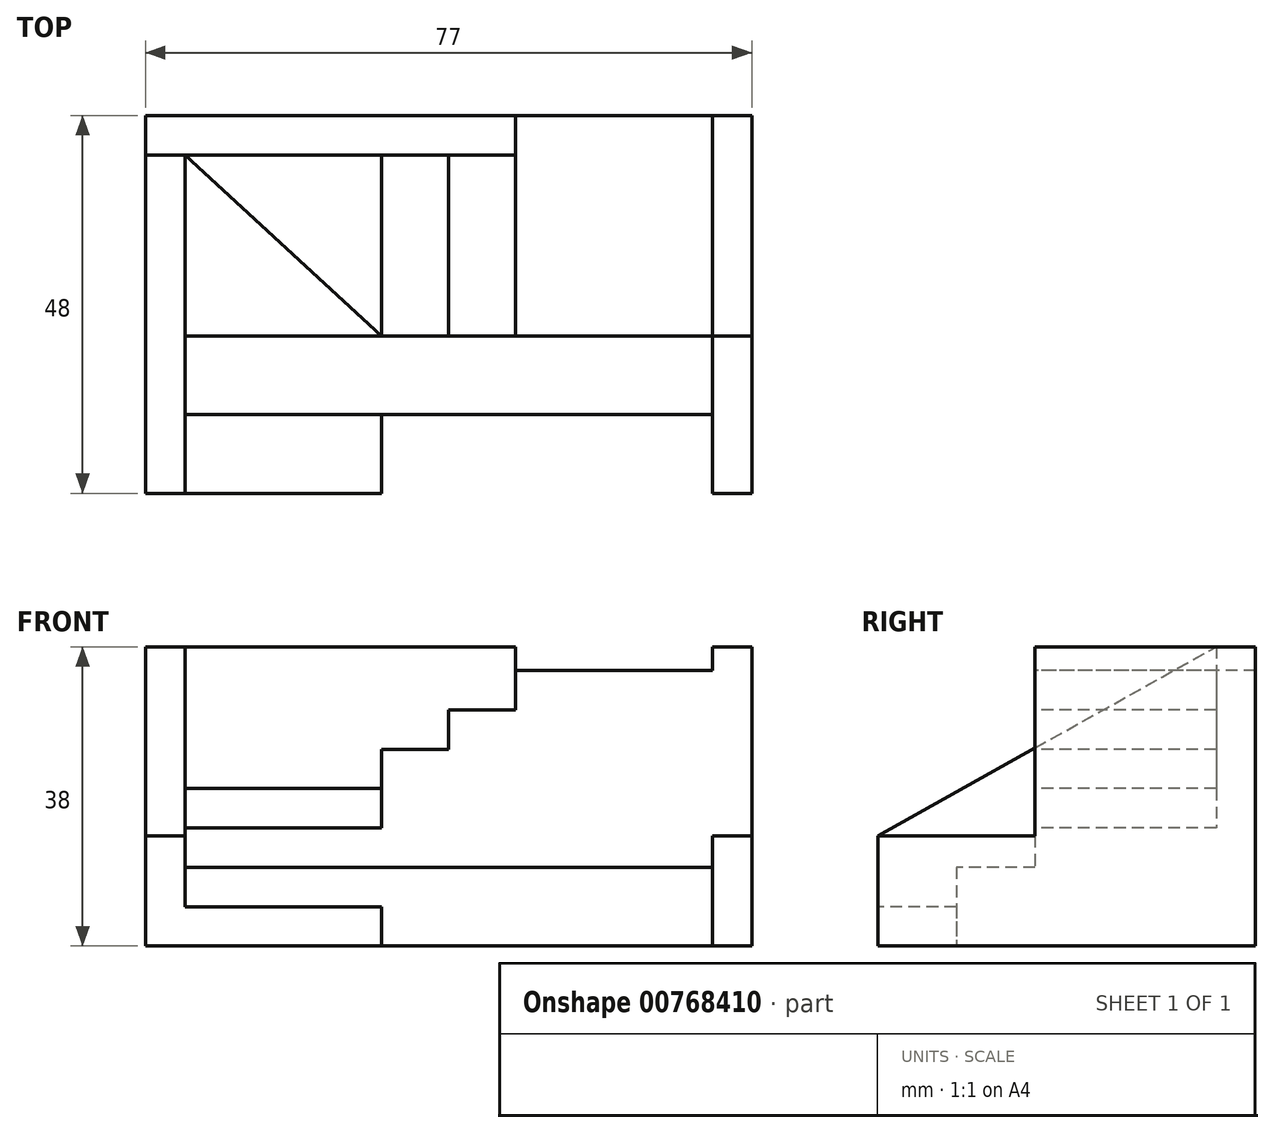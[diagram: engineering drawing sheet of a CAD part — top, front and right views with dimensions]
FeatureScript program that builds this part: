
annotation { "Feature Type Name" : "Feature", "Feature Type Description" : "" }
export const myFeature = defineFeature(function(context is Context, id is Id, definition is map)
    precondition{}
    {
        {
            var Q0;
            Q0=qCreatedBy(makeId("Top.planeOp"),FACE);
            var sketch = newSketch(context, id + "F0", { "sketchPlane" : qUnion([Q0])});
            skLineSegment(sketch, "E0.bottom", {"start": v(38.5, 24) * mm, "end": v(-38.5, 24) * mm});
            skLineSegment(sketch, "E0.top", {"start": v(38.5, -24) * mm, "end": v(33.5, -24) * mm});
            skLineSegment(sketch, "E0.left", {"start": v(38.5, 24) * mm, "end": v(38.5, -24) * mm});
            skLineSegment(sketch, "E0.right", {"start": v(-38.5, 24) * mm, "end": v(-38.5, -24) * mm});
            skPoint(sketch, "E0.middle", {"position": v(0, 0) * mm});
            skLineSegment(sketch, "E1", {"start": v(-33.5, 19) * mm, "end": v(-33.5, -24) * mm});
            skLineSegment(sketch, "E2", {"start": v(-38.5, 19) * mm, "end": v(8.5, 19) * mm});
            skLineSegment(sketch, "E3", {"start": v(-33.5, -14) * mm, "end": v(33.5, -14) * mm});
            skLineSegment(sketch, "E4", {"start": v(-33.5, -4) * mm, "end": v(38.5, -4) * mm});
            skLineSegment(sketch, "E5", {"start": v(-8.5, 19) * mm, "end": v(-8.5, -4) * mm});
            skLineSegment(sketch, "E6", {"start": v(33.5, 24) * mm, "end": v(33.5, -24) * mm});
            skLineSegment(sketch, "E7", {"start": v(8.5, 24) * mm, "end": v(8.5, -4) * mm});
            skLineSegment(sketch, "E8", {"start": v(0, 19) * mm, "end": v(0, -4) * mm});
            skPoint(sketch, "E9.orphan", {"position": v(-38.5, -4) * mm});
            skPoint(sketch, "E10.orphan", {"position": v(0, 24) * mm});
            skPoint(sketch, "E11.orphan", {"position": v(38.5, 19) * mm});
            skPoint(sketch, "E12.orphan", {"position": v(8.5, -24) * mm});
            skLineSegment(sketch, "E13.trimOffspring", {"start": v(-8.5, -24) * mm, "end": v(-38.5, -24) * mm});
            skLineSegment(sketch, "E14.trimOffspring", {"start": v(-8.5, -14) * mm, "end": v(-8.5, -24) * mm});
            skPoint(sketch, "E15.orphan", {"position": v(38.5, -14) * mm});
            skLineSegment(sketch, "E16", {"start": v(-8.5, -4) * mm, "end": v(-33.5, 19) * mm});
            skSolve(sketch);
        }
        {
            var Q0;
            {var subQ0=sQuery(id+"F0.wireOp",EDGE,"E13.trimOffspring");var subQ7=sQuery(id+"F0.wireOp",EDGE,"E0.right");var subQ8=makeQuery(id+"F0.imprint","INTERSECT",VERTEX,{"derivedFrom":[subQ7,subQ0]});Q0=makeQuery(id+"F0.imprint","IMPRINT",FACE,{"disambiguationData":[TD([[makeQuery(id+"F0.imprint","IMPRINT",EDGE,{"disambiguationData":[TD([[subQ8,1.0]])],"derivedFrom":subQ7}),1.0]])]});}
            extrude(context, id + "F1", {"entities" : qUnion([Q0]), "depth" : 38 * mm, "offsetDistance" : 25 * mm});
        }
        {
            var Q0;
            Q0=makeQuery(id+"F1.opExtrude","SWEPT_FACE",FACE,{"disambiguationData":[OSD([sQuery(id+"F0.wireOp",EDGE,"E1")])]});
            var sketch = newSketch(context, id + "F2", { "sketchPlane" : qUnion([Q0])});
            skLineSegment(sketch, "E17", {"start": v(-24, 14) * mm, "end": v(19, 38) * mm});
            skSolve(sketch);
        }
        {
            var Q0;
            {var subQ0=sQuery(id+"F2.wireOp",EDGE,"E17");Q0=makeQuery(id+"F2.imprint","IMPRINT",FACE,{"disambiguationData":[TD([[makeQuery(id+"F2.imprint","IMPRINT",EDGE,{"derivedFrom":subQ0}),1.0]])]});}
            extrude(context, id + "F3", {"entities" : qUnion([Q0]), "operationType" : NewBodyOperationType.REMOVE, "oppositeDirection" : true, "depth" : 25 * mm, "offsetDistance" : 25 * mm});
        }
        {
            var Q0;
            {var subQ2=sQuery(id+"F0.wireOp",EDGE,"E0.right");var subQ4=sQuery(id+"F0.wireOp",EDGE,"E0.bottom");var subQ5=makeQuery(id+"F0.imprint","INTERSECT",VERTEX,{"derivedFrom":[subQ4,subQ2]});Q0=makeQuery(id+"F0.imprint","IMPRINT",FACE,{"disambiguationData":[TD([[makeQuery(id+"F0.imprint","IMPRINT",EDGE,{"disambiguationData":[TD([[subQ5,1.0]])],"derivedFrom":subQ4}),1.0]])]});}
            extrude(context, id + "F4", {"entities" : qUnion([Q0]), "operationType" : NewBodyOperationType.ADD, "depth" : 38 * mm, "offsetDistance" : 25 * mm});
        }
        {
            var Q0;
            {var subQ5=sQuery(id+"F0.wireOp",EDGE,"E14.trimOffspring");Q0=makeQuery(id+"F0.imprint","IMPRINT",FACE,{"disambiguationData":[TD([[makeQuery(id+"F0.imprint","IMPRINT",EDGE,{"derivedFrom":subQ5}),-1.0]])]});}
            extrude(context, id + "F5", {"entities" : qUnion([Q0]), "operationType" : NewBodyOperationType.ADD, "depth" : 5 * mm, "offsetDistance" : 25 * mm});
        }
        {
            var Q0;
            {var subQ1=sQuery(id+"F0.wireOp",EDGE,"E1");var subQ5=sQuery(id+"F0.wireOp",EDGE,"E3");var subQ8=makeQuery(id+"F0.imprint","INTERSECT",VERTEX,{"derivedFrom":[subQ1,subQ5]});Q0=makeQuery(id+"F0.imprint","IMPRINT",FACE,{"disambiguationData":[TD([[makeQuery(id+"F0.imprint","IMPRINT",EDGE,{"disambiguationData":[TD([[subQ8,1.0]])],"derivedFrom":subQ1}),1.0]])]});}
            extrude(context, id + "F6", {"entities" : qUnion([Q0]), "operationType" : NewBodyOperationType.ADD, "depth" : 10 * mm, "offsetDistance" : 25 * mm});
        }
        {
            var Q0;
            {var subQ0=sQuery(id+"F0.wireOp",EDGE,"E5");Q0=makeQuery(id+"F0.imprint","IMPRINT",FACE,{"disambiguationData":[TD([[makeQuery(id+"F0.imprint","IMPRINT",EDGE,{"derivedFrom":subQ0}),1.0]])]});}
            extrude(context, id + "F7", {"entities" : qUnion([Q0]), "operationType" : NewBodyOperationType.ADD, "depth" : 25 * mm, "offsetDistance" : 25 * mm});
        }
        {
            var Q0;
            {var subQ3=sQuery(id+"F0.wireOp",EDGE,"E8");Q0=makeQuery(id+"F0.imprint","IMPRINT",FACE,{"disambiguationData":[TD([[makeQuery(id+"F0.imprint","IMPRINT",EDGE,{"derivedFrom":subQ3}),1.0]])]});}
            extrude(context, id + "F8", {"entities" : qUnion([Q0]), "operationType" : NewBodyOperationType.ADD, "depth" : 30 * mm, "offsetDistance" : 25 * mm});
        }
        {
            var Q0;
            {var subQ2=sQuery(id+"F0.wireOp",EDGE,"E5");Q0=makeQuery(id+"F0.imprint","IMPRINT",FACE,{"disambiguationData":[TD([[makeQuery(id+"F0.imprint","IMPRINT",EDGE,{"derivedFrom":subQ2}),-1.0]])]});}
            extrude(context, id + "F9", {"entities" : qUnion([Q0]), "operationType" : NewBodyOperationType.ADD, "depth" : 20 * mm, "offsetDistance" : 25 * mm});
        }
        {
            var Q0;
            {var subQ0=sQuery(id+"F0.wireOp",EDGE,"E16");Q0=makeQuery(id+"F0.imprint","IMPRINT",FACE,{"disambiguationData":[TD([[makeQuery(id+"F0.imprint","IMPRINT",EDGE,{"derivedFrom":subQ0}),1.0]])]});}
            extrude(context, id + "F10", {"entities" : qUnion([Q0]), "operationType" : NewBodyOperationType.ADD, "depth" : 15 * mm, "offsetDistance" : 25 * mm});
        }
        {
            var Q0;
            {var subQ0=sQuery(id+"F0.wireOp",EDGE,"E6");var subQ1=sQuery(id+"F0.wireOp",EDGE,"E0.bottom");var subQ2=makeQuery(id+"F0.imprint","INTERSECT",VERTEX,{"derivedFrom":[subQ1,subQ0]});Q0=makeQuery(id+"F0.imprint","IMPRINT",FACE,{"disambiguationData":[TD([[makeQuery(id+"F0.imprint","IMPRINT",EDGE,{"disambiguationData":[TD([[subQ2,-1.0]])],"derivedFrom":subQ1}),1.0]])]});}
            extrude(context, id + "F11", {"entities" : qUnion([Q0]), "operationType" : NewBodyOperationType.ADD, "depth" : 35 * mm, "offsetDistance" : 25 * mm});
        }
        {
            var Q0;
            {var subQ0=sQuery(id+"F0.wireOp",EDGE,"E0.left");var subQ1=sQuery(id+"F0.wireOp",EDGE,"E0.bottom");var subQ2=makeQuery(id+"F0.imprint","INTERSECT",VERTEX,{"derivedFrom":[subQ1,subQ0]});Q0=makeQuery(id+"F0.imprint","IMPRINT",FACE,{"disambiguationData":[TD([[makeQuery(id+"F0.imprint","IMPRINT",EDGE,{"disambiguationData":[TD([[subQ2,-1.0]])],"derivedFrom":subQ1}),1.0]])]});}
            extrude(context, id + "F12", {"entities" : qUnion([Q0]), "operationType" : NewBodyOperationType.ADD, "depth" : 38 * mm, "offsetDistance" : 25 * mm});
        }
        {
            var Q0;
            {var subQ6=sQuery(id+"F0.wireOp",EDGE,"E0.top");Q0=makeQuery(id+"F0.imprint","IMPRINT",FACE,{"disambiguationData":[TD([[makeQuery(id+"F0.imprint","IMPRINT",EDGE,{"derivedFrom":subQ6}),-1.0]])]});}
            extrude(context, id + "F13", {"entities" : qUnion([Q0]), "operationType" : NewBodyOperationType.ADD, "depth" : 14 * mm, "offsetDistance" : 25 * mm});
        }
    });
